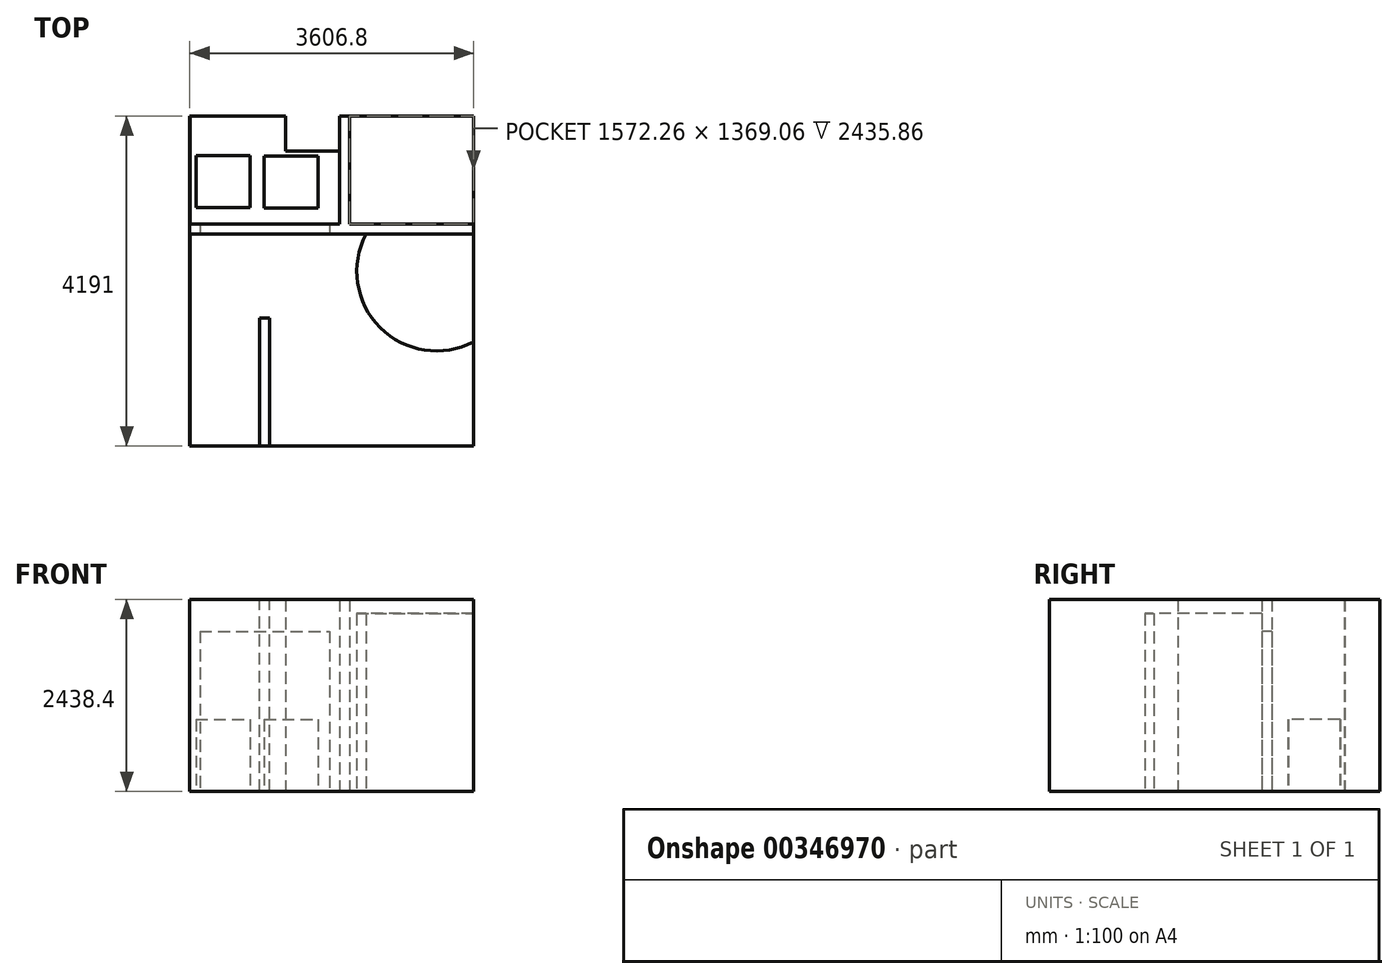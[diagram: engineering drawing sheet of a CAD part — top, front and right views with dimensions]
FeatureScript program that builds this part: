
annotation { "Feature Type Name" : "Feature", "Feature Type Description" : "" }
export const myFeature = defineFeature(function(context is Context, id is Id, definition is map)
    precondition{}
    {
        {
            var Q0;
            Q0=qCreatedBy(makeId("Top.planeOp"),FACE);
            var sketch = newSketch(context, id + "F0", { "sketchPlane" : qUnion([Q0])});
            skLineSegment(sketch, "E0.bottom", {"start": v(-1784.47, 1899.05) * mm, "end": v(1822.33, 1899.05) * mm, "construction": true});
            skLineSegment(sketch, "E0.top", {"start": v(-1784.47, -2291.95) * mm, "end": v(1822.33, -2291.95) * mm, "construction": true});
            skLineSegment(sketch, "E0.left", {"start": v(-1784.47, 1899.05) * mm, "end": v(-1784.47, -2291.95) * mm, "construction": true});
            skLineSegment(sketch, "E0.right", {"start": v(1822.33, 1899.05) * mm, "end": v(1822.33, -2291.95) * mm, "construction": true});
            skLineSegment(sketch, "E1.bottom", {"start": v(-1784.47, 1899.05) * mm, "end": v(1822.33, 1899.05) * mm});
            skLineSegment(sketch, "E1.top", {"start": v(-1784.47, -2291.95) * mm, "end": v(1822.33, -2291.95) * mm});
            skLineSegment(sketch, "E1.left", {"start": v(-1784.47, 1899.05) * mm, "end": v(-1784.47, -2291.95) * mm});
            skLineSegment(sketch, "E1.right", {"start": v(1822.33, 1899.05) * mm, "end": v(1822.33, -2291.95) * mm});
            skSolve(sketch);
        }
        {
            var Q0;
            Q0=qCreatedBy(makeId("Top.planeOp"),FACE);
            var sketch = newSketch(context, id + "F1", { "sketchPlane" : qUnion([Q0])});
            skLineSegment(sketch, "E2.bottom", {"start": v(-565.27, 1899.05) * mm, "end": v(120.53, 1899.05) * mm});
            skLineSegment(sketch, "E2.top", {"start": v(-565.27, 1454.55) * mm, "end": v(120.53, 1454.55) * mm});
            skLineSegment(sketch, "E2.left", {"start": v(-565.27, 1899.05) * mm, "end": v(-565.27, 1454.55) * mm});
            skLineSegment(sketch, "E2.right", {"start": v(120.53, 1899.05) * mm, "end": v(120.53, 1454.55) * mm});
            skSolve(sketch);
        }
        {
            var Q0;
            Q0=qCreatedBy(makeId("Top.planeOp"),FACE);
            var sketch = newSketch(context, id + "F2", { "sketchPlane" : qUnion([Q0])});
            skLineSegment(sketch, "E3.bottom", {"start": v(1822.33, 400.45) * mm, "end": v(453.33, 400.45) * mm});
            skArc(sketch, "E4", {"start": v(453.33, 400.45) * mm, "mid": v(633.69, -788.2) * mm, "end": v(1822.33, -968.55) * mm});
            skLineSegment(sketch, "E5", {"start": v(1822.33, 400.45) * mm, "end": v(1822.33, -968.55) * mm});
            skSolve(sketch);
        }
        {
            var Q0;
            Q0=makeQuery(id+"F0.imprint","IMPRINT",FACE,{"disambiguationData":[TD([[makeQuery(id+"F0.imprint","IMPRINT",EDGE,{"derivedFrom":sQuery(id+"F0.wireOp",EDGE,"E1.bottom")}),-1.0]])]});
            extrude(context, id + "F3", {"entities" : qUnion([Q0]), "depth" : 2438.4 * mm});
        }
        {
            var Q0;
            Q0 = qSketchRegion(id + "F1", true);
            extrude(context, id + "F4", {"entities" : qUnion([Q0]), "operationType" : NewBodyOperationType.REMOVE, "depth" : 2438.4 * mm});
        }
        {
            var Q0;
            Q0=makeQuery(id+"F3.opExtrude","CAP_FACE",FACE,{"disambiguationData":[OSD([sQuery(id+"F0.wireOp",EDGE,"E1.bottom"),sQuery(id+"F0.wireOp",EDGE,"E1.top"),sQuery(id+"F0.wireOp",EDGE,"E1.left"),sQuery(id+"F0.wireOp",EDGE,"E1.right")])],"isStart":false});
            shell(context, id + "F5", {"entities" : qUnion([Q0]), "thickness" : 2.54 * mm});
        }
        {
            var Q0;
            Q0=makeQuery(id+"F2.imprint","IMPRINT",FACE,{"disambiguationData":[TD([[makeQuery(id+"F2.imprint","IMPRINT",EDGE,{"derivedFrom":sQuery(id+"F2.wireOp",EDGE,"E3.bottom")}),1.0]])]});
            extrude(context, id + "F6", {"entities" : qUnion([Q0]), "operationType" : NewBodyOperationType.ADD, "depth" : 2260 * mm});
        }
        {
            var Q0;
            Q0=qCreatedBy(makeId("Top.planeOp"),FACE);
            var sketch = newSketch(context, id + "F7", { "sketchPlane" : qUnion([Q0])});
            skLineSegment(sketch, "E6.bottom", {"start": v(-895.47, -2291.95) * mm, "end": v(-768.47, -2291.95) * mm});
            skLineSegment(sketch, "E6.top", {"start": v(-895.47, -666.35) * mm, "end": v(-768.47, -666.35) * mm});
            skLineSegment(sketch, "E6.left", {"start": v(-895.47, -2291.95) * mm, "end": v(-895.47, -666.35) * mm});
            skLineSegment(sketch, "E6.right", {"start": v(-768.47, -2291.95) * mm, "end": v(-768.47, -666.35) * mm});
            skSolve(sketch);
        }
        {
            var Q0;
            Q0 = qSketchRegion(id + "F7", true);
            extrude(context, id + "F8", {"entities" : qUnion([Q0]), "operationType" : NewBodyOperationType.ADD, "depth" : 2438.4 * mm});
        }
        {
            var Q0;
            Q0=qCreatedBy(makeId("Top.planeOp"),FACE);
            var sketch = newSketch(context, id + "F9", { "sketchPlane" : qUnion([Q0])});
            skLineSegment(sketch, "E7.bottom", {"start": v(-1706.72, 1398.42) * mm, "end": v(-1020.92, 1398.42) * mm});
            skLineSegment(sketch, "E7.top", {"start": v(-1706.72, 738.02) * mm, "end": v(-1020.92, 738.02) * mm});
            skLineSegment(sketch, "E7.left", {"start": v(-1706.72, 1398.42) * mm, "end": v(-1706.72, 738.02) * mm});
            skLineSegment(sketch, "E7.right", {"start": v(-1020.92, 1398.42) * mm, "end": v(-1020.92, 738.02) * mm});
            skLineSegment(sketch, "E8.bottom", {"start": v(-838.07, 1392.47) * mm, "end": v(-152.27, 1392.47) * mm});
            skLineSegment(sketch, "E8.top", {"start": v(-838.07, 732.07) * mm, "end": v(-152.27, 732.07) * mm});
            skLineSegment(sketch, "E8.left", {"start": v(-838.07, 1392.47) * mm, "end": v(-838.07, 732.07) * mm});
            skLineSegment(sketch, "E8.right", {"start": v(-152.27, 1392.47) * mm, "end": v(-152.27, 732.07) * mm});
            skSolve(sketch);
        }
        {
            var Q0;
            Q0 = qSketchRegion(id + "F9", true);
            extrude(context, id + "F10", {"entities" : qUnion([Q0]), "operationType" : NewBodyOperationType.ADD, "depth" : 914.4 * mm});
        }
        {
            var Q0;
            Q0=qCreatedBy(makeId("Top.planeOp"),FACE);
            var sketch = newSketch(context, id + "F11", { "sketchPlane" : qUnion([Q0])});
            skLineSegment(sketch, "E9.bottom", {"start": v(120.53, 1899.05) * mm, "end": v(247.53, 1899.05) * mm});
            skLineSegment(sketch, "E9.top", {"start": v(120.53, 527.45) * mm, "end": v(247.53, 527.45) * mm});
            skLineSegment(sketch, "E9.left", {"start": v(120.53, 1899.05) * mm, "end": v(120.53, 527.45) * mm});
            skLineSegment(sketch, "E9.right", {"start": v(247.53, 1899.05) * mm, "end": v(247.53, 527.45) * mm});
            skLineSegment(sketch, "E10.bottom", {"start": v(120.53, 527.45) * mm, "end": v(1822.33, 527.45) * mm});
            skLineSegment(sketch, "E10.top", {"start": v(120.53, 400.45) * mm, "end": v(1822.33, 400.45) * mm});
            skLineSegment(sketch, "E10.left", {"start": v(120.53, 527.45) * mm, "end": v(120.53, 400.45) * mm});
            skLineSegment(sketch, "E10.right", {"start": v(1822.33, 527.45) * mm, "end": v(1822.33, 400.45) * mm});
            skLineSegment(sketch, "E11.bottom", {"start": v(120.53, 527.45) * mm, "end": v(-1781.93, 527.45) * mm});
            skLineSegment(sketch, "E11.top", {"start": v(120.53, 400.45) * mm, "end": v(-1781.93, 400.45) * mm});
            skLineSegment(sketch, "E11.right", {"start": v(-1781.93, 527.45) * mm, "end": v(-1781.93, 400.45) * mm});
            skSolve(sketch);
        }
        {
            var Q0;
            Q0 = qSketchRegion(id + "F11", true);
            extrude(context, id + "F12", {"entities" : qUnion([Q0]), "operationType" : NewBodyOperationType.ADD, "depth" : 2438.4 * mm});
        }
        {
            var Q0;
            Q0=makeQuery(id+"F12.opExtrude","SWEPT_FACE",FACE,{"disambiguationData":[OSD([sQuery(id+"F11.wireOp",EDGE,"E10.top"),sQuery(id+"F11.wireOp",EDGE,"E11.top")])]});
            var sketch = newSketch(context, id + "F13", { "sketchPlane" : qUnion([Q0])});
            skLineSegment(sketch, "E12.bottom", {"start": v(-1654.93, 2034.54) * mm, "end": v(-6.47, 2034.54) * mm});
            skLineSegment(sketch, "E12.top", {"start": v(-1654.93, 2.54) * mm, "end": v(-6.47, 2.54) * mm});
            skLineSegment(sketch, "E12.left", {"start": v(-1654.93, 2034.54) * mm, "end": v(-1654.93, 2.54) * mm});
            skLineSegment(sketch, "E12.right", {"start": v(-6.47, 2034.54) * mm, "end": v(-6.47, 2.54) * mm});
            skSolve(sketch);
        }
        {
            var Q0;
            Q0=makeQuery(id+"F13.imprint","IMPRINT",FACE,{"disambiguationData":[TD([[makeQuery(id+"F13.imprint","IMPRINT",EDGE,{"derivedFrom":sQuery(id+"F13.wireOp",EDGE,"E12.bottom")}),-1.0]])]});
            extrude(context, id + "F14", {"entities" : qUnion([Q0]), "operationType" : NewBodyOperationType.REMOVE, "oppositeDirection" : true, "depth" : 127 * mm});
        }
    });
